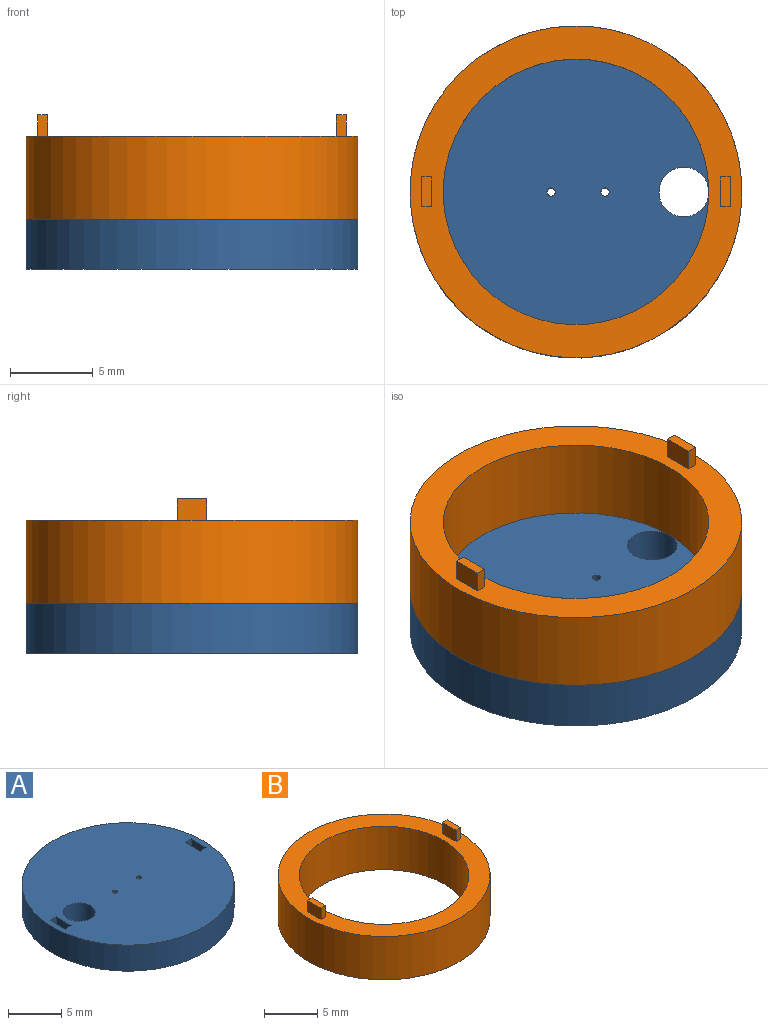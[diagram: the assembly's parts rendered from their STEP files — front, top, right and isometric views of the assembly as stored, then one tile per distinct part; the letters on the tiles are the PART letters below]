
ASSEMBLY  parts=2 mates=1
PART A: 16 faces, bbox 20x20x3 mm
  f0: plane 2x1.5mm, normal (1,0,0), area 3mm2, adj f1,f6,f12,f15
  f1: plane 1.5x0.8mm, normal (0,-1,0), area 1.2mm2, adj f0,f2,f12,f15
  f2: plane 2x1.5mm, normal (-1,0,0), area 3mm2, adj f1,f6,f12,f15
  f3: plane 2x1.5mm, normal (1,0,0), area 3mm2, adj f4,f7,f12,f14
  f4: plane 1.5x0.8mm, normal (0,-1,0), area 1.2mm2, adj f3,f5,f12,f14
  f5: plane 2x1.5mm, normal (-1,0,0), area 3mm2, adj f4,f7,f12,f14
  f6: plane 1.5x0.8mm, normal (0,1,0), area 1.2mm2, adj f0,f2,f12,f15
  f7: plane 1.5x0.8mm, normal (0,1,0), area 1.2mm2, adj f3,f5,f12,f14
  f8: cylinder r=0.25mm len=3mm, axis (0,0,-1), area 4.7mm2, adj f12,f13
  f9: cylinder r=0.25mm len=3mm, axis (0,0,-1), area 4.7mm2, adj f12,f13
  f10: cylinder r=1.5mm len=3mm, axis (0,0,-1), area 28.3mm2, adj f12,f13
  f11: cylinder r=10mm len=20mm, axis (0,0,-1), area 188.5mm2, adj f12,f13
  f12: plane 20x20mm, normal (0,0,1), area 303.5mm2, adj f0,f1,f2,f3,f4,f5,f6,f7
  f13: plane 20x20mm, normal (0,0,-1), area 306.7mm2, adj f8,f9,f10,f11
  f14: plane 2x0.8mm, normal (0,0,1), area 1.6mm2, adj f3,f4,f5,f7
  f15: plane 2x0.8mm, normal (0,0,1), area 1.6mm2, adj f0,f1,f2,f6
PART B: 14 faces, bbox 20x20x6.3 mm
  f0: plane 1.8x1.3mm, normal (-1,0,0), area 2.3mm2, adj f1,f3,f4,f12
  f1: plane 1.3x0.6mm, normal (0,-1,0), area 0.8mm2, adj f0,f2,f4,f12
  f2: plane 1.8x1.3mm, normal (1,0,0), area 2.3mm2, adj f1,f3,f4,f12
  f3: plane 1.3x0.6mm, normal (0,1,0), area 0.8mm2, adj f0,f2,f4,f12
  f4: plane 1.8x0.6mm, normal (0,0,1), area 1.1mm2, adj f0,f1,f2,f3
  f5: plane 1.8x1.3mm, normal (-1,0,0), area 2.3mm2, adj f6,f8,f9,f12
  f6: plane 1.3x0.6mm, normal (0,-1,0), area 0.8mm2, adj f5,f7,f9,f12
  f7: plane 1.8x1.3mm, normal (1,0,0), area 2.3mm2, adj f6,f8,f9,f12
  f8: plane 1.3x0.6mm, normal (0,1,0), area 0.8mm2, adj f5,f7,f9,f12
  f9: plane 1.8x0.6mm, normal (0,0,1), area 1.1mm2, adj f5,f6,f7,f8
  f10: cylinder r=8mm len=16mm, axis (0,0,-1), area 251.3mm2, adj f12,f13
  f11: cylinder r=10mm len=20mm, axis (0,0,-1), area 314.2mm2, adj f12,f13
  f12: plane 20x20mm, normal (0,0,1), area 110.9mm2, adj f0,f1,f2,f3,f5,f6,f7,f8
  f13: plane 20x20mm, normal (0,0,-1), area 113.1mm2, adj f10,f11
PLACE A rot(axis=(0,1,0),180deg) t=(-12.74,2.2,4.36)mm
PLACE B t=(-12.74,2.2,4.36)mm
MATE fastened A.f11 <-> B.f10  axis (0,0,1) through (-12.74,2.2,4.36)mm
